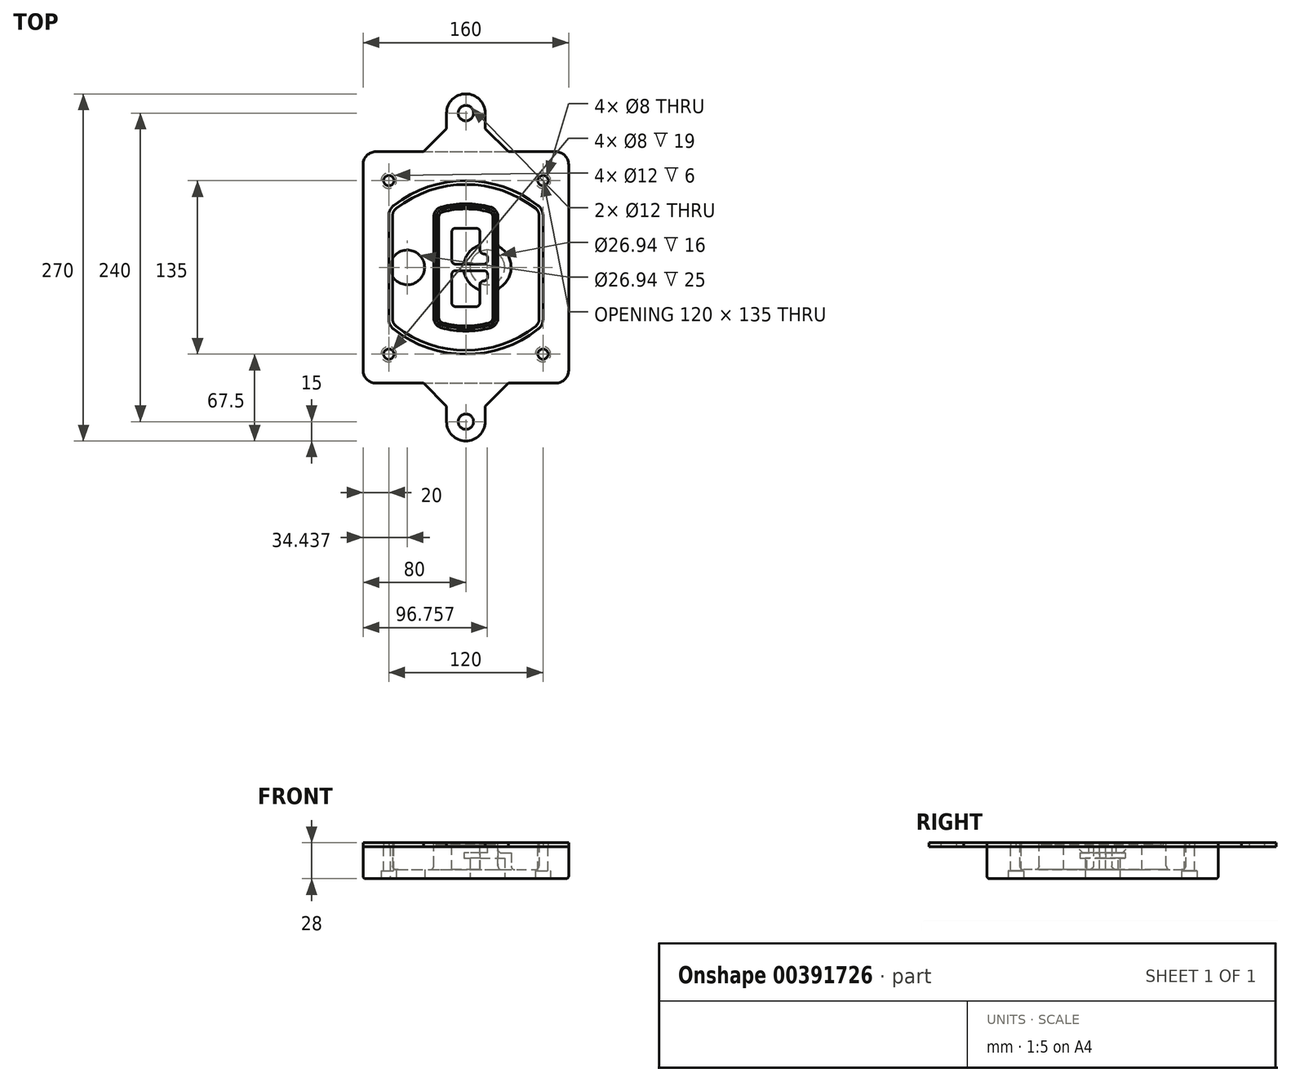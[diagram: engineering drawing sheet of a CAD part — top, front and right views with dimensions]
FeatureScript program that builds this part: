
annotation { "Feature Type Name" : "Feature", "Feature Type Description" : "" }
export const myFeature = defineFeature(function(context is Context, id is Id, definition is map)
    precondition{}
    {
        {
            var Q0;
            Q0=qCreatedBy(makeId("Top.planeOp"),FACE);
            var sketch = newSketch(context, id + "F0", { "sketchPlane" : qUnion([Q0])});
            skPoint(sketch, "E0.rect.middle", {"position": v(0, 0) * mm});
            skLineSegment(sketch, "E1.bottom", {"start": v(-70, -90) * mm, "end": v(70, -90) * mm});
            skLineSegment(sketch, "E1.top", {"start": v(-70, 90) * mm, "end": v(70, 90) * mm});
            skLineSegment(sketch, "E1.left", {"start": v(-80, -80) * mm, "end": v(-80, 80) * mm});
            skLineSegment(sketch, "E1.right", {"start": v(80, -80) * mm, "end": v(80, 80) * mm});
            skLineSegment(sketch, "E2", {"start": v(-80, 90) * mm, "end": v(80, -90) * mm, "construction": true});
            skLineSegment(sketch, "E3", {"start": v(80, 90) * mm, "end": v(-80, -90) * mm, "construction": true});
            skCircle(sketch, "E4", {"center": v(-60, 67.5) * mm, "radius": 4 * mm});
            skCircle(sketch, "E5", {"center": v(60, 67.5) * mm, "radius": 4 * mm});
            skCircle(sketch, "E6", {"center": v(60, -67.5) * mm, "radius": 4 * mm});
            skCircle(sketch, "E7", {"center": v(-60, -67.5) * mm, "radius": 4 * mm});
            skLineSegment(sketch, "E8", {"start": v(-60, 67.5) * mm, "end": v(60, 67.5) * mm, "construction": true});
            skLineSegment(sketch, "E9", {"start": v(60, 67.5) * mm, "end": v(60, -67.5) * mm, "construction": true});
            skLineSegment(sketch, "E10", {"start": v(60, -67.5) * mm, "end": v(-60, -67.5) * mm, "construction": true});
            skLineSegment(sketch, "E11", {"start": v(-60, -67.5) * mm, "end": v(-60, 67.5) * mm, "construction": true});
            skLineSegment(sketch, "E12", {"start": v(-60, 40.3) * mm, "end": v(-60, -40.3) * mm});
            skLineSegment(sketch, "E13", {"start": v(60, 40.3) * mm, "end": v(60, -40.3) * mm});
            skArc(sketch, "E14", {"start": v(56.15, 48.18) * mm, "mid": v(0, 67.5) * mm, "end": v(-56.15, 48.18) * mm});
            skArc(sketch, "E15", {"start": v(-56.15, -48.18) * mm, "mid": v(0, -67.5) * mm, "end": v(56.15, -48.18) * mm});
            skLineSegment(sketch, "E16", {"start": v(-60, 0) * mm, "end": v(60, 0) * mm, "construction": true});
            skPoint(sketch, "E17.visualSharp", {"position": v(-60, -45) * mm});
            skArc(sketch, "E17.filletArc", {"start": v(-60, -40.3) * mm, "mid": v(-58.99, -44.68) * mm, "end": v(-56.15, -48.18) * mm});
            skPoint(sketch, "E18.visualSharp", {"position": v(-60, 45) * mm});
            skArc(sketch, "E18.filletArc", {"start": v(-56.15, 48.18) * mm, "mid": v(-58.99, 44.68) * mm, "end": v(-60, 40.3) * mm});
            skPoint(sketch, "E19.visualSharp", {"position": v(60, 45) * mm});
            skArc(sketch, "E19.filletArc", {"start": v(60, 40.3) * mm, "mid": v(58.99, 44.68) * mm, "end": v(56.15, 48.18) * mm});
            skPoint(sketch, "E20.visualSharp", {"position": v(60, -45) * mm});
            skArc(sketch, "E20.filletArc", {"start": v(56.15, -48.18) * mm, "mid": v(58.99, -44.68) * mm, "end": v(60, -40.3) * mm});
            skPoint(sketch, "E21.visualSharp", {"position": v(-80, 90) * mm});
            skArc(sketch, "E21.filletArc", {"start": v(-70, 90) * mm, "mid": v(-77.07, 87.07) * mm, "end": v(-80, 80) * mm});
            skPoint(sketch, "E22.visualSharp", {"position": v(80, 90) * mm});
            skArc(sketch, "E22.filletArc", {"start": v(80, 80) * mm, "mid": v(77.07, 87.07) * mm, "end": v(70, 90) * mm});
            skPoint(sketch, "E23.visualSharp", {"position": v(80, -90) * mm});
            skArc(sketch, "E23.filletArc", {"start": v(70, -90) * mm, "mid": v(77.07, -87.07) * mm, "end": v(80, -80) * mm});
            skPoint(sketch, "E24.visualSharp", {"position": v(-80, -90) * mm});
            skArc(sketch, "E24.filletArc", {"start": v(-80, -80) * mm, "mid": v(-77.07, -87.07) * mm, "end": v(-70, -90) * mm});
            skArc(sketch, "E25.0", {"start": v(57, 40.3) * mm, "mid": v(56.3, 43.36) * mm, "end": v(54.3, 45.81) * mm});
            skLineSegment(sketch, "E25.1", {"start": v(57, 40.3) * mm, "end": v(57, -40.3) * mm});
            skArc(sketch, "E25.2", {"start": v(54.3, -45.81) * mm, "mid": v(56.3, -43.36) * mm, "end": v(57, -40.3) * mm});
            skArc(sketch, "E25.3", {"start": v(-54.3, -45.81) * mm, "mid": v(0, -64.5) * mm, "end": v(54.3, -45.81) * mm});
            skArc(sketch, "E25.4", {"start": v(-57, -40.3) * mm, "mid": v(-56.3, -43.36) * mm, "end": v(-54.3, -45.81) * mm});
            skArc(sketch, "E25.5", {"start": v(54.3, 45.81) * mm, "mid": v(0, 64.5) * mm, "end": v(-54.3, 45.81) * mm});
            skLineSegment(sketch, "E25.6", {"start": v(-57, 40.3) * mm, "end": v(-57, -40.3) * mm});
            skArc(sketch, "E25.7", {"start": v(-54.3, 45.81) * mm, "mid": v(-56.3, 43.36) * mm, "end": v(-57, 40.3) * mm});
            skArc(sketch, "E26.0", {"start": v(-58.62, 51.33) * mm, "mid": v(-62.58, 46.43) * mm, "end": v(-64, 40.3) * mm});
            skArc(sketch, "E26.1", {"start": v(58.62, 51.33) * mm, "mid": v(0, 71.5) * mm, "end": v(-58.62, 51.33) * mm});
            skArc(sketch, "E26.2", {"start": v(64, 40.3) * mm, "mid": v(62.58, 46.43) * mm, "end": v(58.62, 51.33) * mm});
            skLineSegment(sketch, "E26.3", {"start": v(64, 40.3) * mm, "end": v(64, -40.3) * mm});
            skArc(sketch, "E26.4", {"start": v(58.62, -51.33) * mm, "mid": v(62.58, -46.43) * mm, "end": v(64, -40.3) * mm});
            skLineSegment(sketch, "E26.5", {"start": v(-64, 40.3) * mm, "end": v(-64, -40.3) * mm});
            skArc(sketch, "E26.6", {"start": v(-58.62, -51.33) * mm, "mid": v(0, -71.5) * mm, "end": v(58.62, -51.33) * mm});
            skArc(sketch, "E26.7", {"start": v(-64, -40.3) * mm, "mid": v(-62.58, -46.43) * mm, "end": v(-58.62, -51.33) * mm});
            skSolve(sketch);
        }
        {
            var Q0;
            Q0=makeQuery(id+"F0.imprint","IMPRINT",FACE,{"disambiguationData":[TD([[makeQuery(id+"F0.imprint","IMPRINT",EDGE,{"derivedFrom":sQuery(id+"F0.wireOp",EDGE,"E1.bottom")}),1.0]])]});
            var Q1;
            Q1=makeQuery(id+"F0.imprint","IMPRINT",FACE,{"disambiguationData":[TD([[makeQuery(id+"F0.imprint","IMPRINT",EDGE,{"derivedFrom":sQuery(id+"F0.wireOp",EDGE,"E12")}),1.0]])]});
            var Q2;
            Q2=makeQuery(id+"F0.imprint","IMPRINT",FACE,{"disambiguationData":[TD([[makeQuery(id+"F0.imprint","IMPRINT",EDGE,{"derivedFrom":sQuery(id+"F0.wireOp",EDGE,"E25.0")}),1.0]])]});
            var Q3;
            Q3=makeQuery(id+"F0.imprint","IMPRINT",FACE,{"disambiguationData":[TD([[makeQuery(id+"F0.imprint","IMPRINT",EDGE,{"derivedFrom":sQuery(id+"F0.wireOp",EDGE,"E12")}),-1.0]])]});
            extrude(context, id + "F1", {"entities" : qUnion([Q0, Q1, Q2, Q3]), "oppositeDirection" : true, "depth" : 25 * mm});
        }
        {
            var Q0;
            Q0=makeQuery(id+"F0.imprint","IMPRINT",FACE,{"disambiguationData":[TD([[makeQuery(id+"F0.imprint","IMPRINT",EDGE,{"derivedFrom":sQuery(id+"F0.wireOp",EDGE,"E12")}),1.0]])]});
            extrude(context, id + "F2", {"entities" : qUnion([Q0]), "operationType" : NewBodyOperationType.ADD, "depth" : 3 * mm});
        }
        {
            var Q0;
            Q0=makeQuery(id+"F0.imprint","IMPRINT",FACE,{"disambiguationData":[TD([[makeQuery(id+"F0.imprint","IMPRINT",EDGE,{"derivedFrom":sQuery(id+"F0.wireOp",EDGE,"E25.0")}),1.0]])]});
            extrude(context, id + "F3", {"entities" : qUnion([Q0]), "operationType" : NewBodyOperationType.REMOVE, "oppositeDirection" : true, "depth" : 18 * mm});
        }
        {
            var Q0;
            Q0=makeQuery(id+"F2.opExtrude","CAP_FACE",FACE,{"disambiguationData":[OSD([sQuery(id+"F0.wireOp",EDGE,"E12"),sQuery(id+"F0.wireOp",EDGE,"E13"),sQuery(id+"F0.wireOp",EDGE,"E14"),sQuery(id+"F0.wireOp",EDGE,"E15"),sQuery(id+"F0.wireOp",EDGE,"E17.filletArc"),sQuery(id+"F0.wireOp",EDGE,"E18.filletArc"),sQuery(id+"F0.wireOp",EDGE,"E19.filletArc"),sQuery(id+"F0.wireOp",EDGE,"E20.filletArc"),sQuery(id+"F0.wireOp",EDGE,"E25.0"),sQuery(id+"F0.wireOp",EDGE,"E25.1"),sQuery(id+"F0.wireOp",EDGE,"E25.2"),sQuery(id+"F0.wireOp",EDGE,"E25.3"),sQuery(id+"F0.wireOp",EDGE,"E25.4"),sQuery(id+"F0.wireOp",EDGE,"E25.5"),sQuery(id+"F0.wireOp",EDGE,"E25.6"),sQuery(id+"F0.wireOp",EDGE,"E25.7")])],"isStart":false});
            var sketch = newSketch(context, id + "F4", { "sketchPlane" : qUnion([Q0])});
            skArc(sketch, "E27.0", {"start": v(-19.08, -46.97) * mm, "mid": v(0, -49.5) * mm, "end": v(19.08, -46.97) * mm});
            skArc(sketch, "E28.0", {"start": v(19.08, 46.97) * mm, "mid": v(0, 49.5) * mm, "end": v(-19.08, 46.97) * mm});
            skLineSegment(sketch, "E29", {"start": v(-25, 39.25) * mm, "end": v(-25, -39.25) * mm});
            skLineSegment(sketch, "E30", {"start": v(25, 39.25) * mm, "end": v(25, -39.25) * mm});
            skLineSegment(sketch, "E31", {"start": v(-25, 45.1) * mm, "end": v(25, 45.1) * mm, "construction": true});
            skLineSegment(sketch, "E32", {"start": v(-25, -45.1) * mm, "end": v(25, -45.1) * mm, "construction": true});
            skPoint(sketch, "E33.visualSharp", {"position": v(-25, 45.1) * mm});
            skArc(sketch, "E33.filletArc", {"start": v(-19.08, 46.97) * mm, "mid": v(-23.35, 44.11) * mm, "end": v(-25, 39.25) * mm});
            skPoint(sketch, "E34.visualSharp", {"position": v(25, 45.1) * mm});
            skArc(sketch, "E34.filletArc", {"start": v(25, 39.25) * mm, "mid": v(23.35, 44.11) * mm, "end": v(19.08, 46.97) * mm});
            skPoint(sketch, "E35.visualSharp", {"position": v(25, -45.1) * mm});
            skArc(sketch, "E35.filletArc", {"start": v(19.08, -46.97) * mm, "mid": v(23.35, -44.11) * mm, "end": v(25, -39.25) * mm});
            skPoint(sketch, "E36.visualSharp", {"position": v(-25, -45.1) * mm});
            skArc(sketch, "E36.filletArc", {"start": v(-25, -39.25) * mm, "mid": v(-23.35, -44.11) * mm, "end": v(-19.08, -46.97) * mm});
            skArc(sketch, "E37.0", {"start": v(54.3, 45.81) * mm, "mid": v(0, 64.5) * mm, "end": v(-54.3, 45.81) * mm});
            skArc(sketch, "E37.1", {"start": v(-54.3, 45.81) * mm, "mid": v(-56.3, 43.36) * mm, "end": v(-57, 40.3) * mm});
            skLineSegment(sketch, "E37.2", {"start": v(-57, 40.3) * mm, "end": v(-57, -40.3) * mm});
            skArc(sketch, "E37.3", {"start": v(-57, -40.3) * mm, "mid": v(-56.3, -43.36) * mm, "end": v(-54.3, -45.81) * mm});
            skArc(sketch, "E37.4", {"start": v(-54.3, -45.81) * mm, "mid": v(0, -64.5) * mm, "end": v(54.3, -45.81) * mm});
            skArc(sketch, "E37.5", {"start": v(54.3, -45.81) * mm, "mid": v(56.3, -43.36) * mm, "end": v(57, -40.3) * mm});
            skLineSegment(sketch, "E37.6", {"start": v(57, 40.3) * mm, "end": v(57, -40.3) * mm});
            skArc(sketch, "E37.7", {"start": v(57, 40.3) * mm, "mid": v(56.3, 43.36) * mm, "end": v(54.3, 45.81) * mm});
            skLineSegment(sketch, "E38.0", {"start": v(23, 39.25) * mm, "end": v(23, -39.25) * mm});
            skArc(sketch, "E38.1", {"start": v(18.56, -45.04) * mm, "mid": v(21.76, -42.9) * mm, "end": v(23, -39.25) * mm});
            skArc(sketch, "E38.2", {"start": v(-18.56, -45.04) * mm, "mid": v(0, -47.5) * mm, "end": v(18.56, -45.04) * mm});
            skArc(sketch, "E38.3", {"start": v(-23, -39.25) * mm, "mid": v(-21.76, -42.9) * mm, "end": v(-18.56, -45.04) * mm});
            skLineSegment(sketch, "E38.4", {"start": v(-23, 39.25) * mm, "end": v(-23, -39.25) * mm});
            skArc(sketch, "E38.5", {"start": v(23, 39.25) * mm, "mid": v(21.76, 42.9) * mm, "end": v(18.56, 45.04) * mm});
            skArc(sketch, "E38.6", {"start": v(-18.56, 45.04) * mm, "mid": v(-21.76, 42.9) * mm, "end": v(-23, 39.25) * mm});
            skArc(sketch, "E38.7", {"start": v(18.56, 45.04) * mm, "mid": v(0, 47.5) * mm, "end": v(-18.56, 45.04) * mm});
            skArc(sketch, "E39.0", {"start": v(21, 39.25) * mm, "mid": v(20.18, 41.68) * mm, "end": v(18.04, 43.1) * mm});
            skLineSegment(sketch, "E39.1", {"start": v(21, 39.25) * mm, "end": v(21, -39.25) * mm});
            skArc(sketch, "E39.2", {"start": v(18.04, -43.1) * mm, "mid": v(20.18, -41.68) * mm, "end": v(21, -39.25) * mm});
            skArc(sketch, "E39.3", {"start": v(-18.04, -43.1) * mm, "mid": v(0, -45.5) * mm, "end": v(18.04, -43.1) * mm});
            skArc(sketch, "E39.4", {"start": v(-21, -39.25) * mm, "mid": v(-20.18, -41.68) * mm, "end": v(-18.04, -43.1) * mm});
            skArc(sketch, "E39.5", {"start": v(18.04, 43.1) * mm, "mid": v(0, 45.5) * mm, "end": v(-18.04, 43.1) * mm});
            skLineSegment(sketch, "E39.6", {"start": v(-21, 39.25) * mm, "end": v(-21, -39.25) * mm});
            skArc(sketch, "E39.7", {"start": v(-18.04, 43.1) * mm, "mid": v(-20.18, 41.68) * mm, "end": v(-21, 39.25) * mm});
            skLineSegment(sketch, "E40", {"start": v(-25, 0) * mm, "end": v(25, 0) * mm, "construction": true});
            skLineSegment(sketch, "E41", {"start": v(-11, 5.5) * mm, "end": v(-11, 27.5) * mm});
            skLineSegment(sketch, "E42", {"start": v(-8, 30.5) * mm, "end": v(8, 30.5) * mm});
            skLineSegment(sketch, "E43", {"start": v(11, 27.5) * mm, "end": v(11, 13.5) * mm});
            skLineSegment(sketch, "E44", {"start": v(14, 10.5) * mm, "end": v(14, 10.5) * mm});
            skLineSegment(sketch, "E45", {"start": v(17, 7.5) * mm, "end": v(17, 5.5) * mm});
            skLineSegment(sketch, "E46", {"start": v(14, 2.5) * mm, "end": v(-8, 2.5) * mm});
            skPoint(sketch, "E47.visualSharp", {"position": v(-11, 30.5) * mm});
            skArc(sketch, "E47.filletArc", {"start": v(-8, 30.5) * mm, "mid": v(-10.12, 29.62) * mm, "end": v(-11, 27.5) * mm});
            skPoint(sketch, "E48.visualSharp", {"position": v(11, 30.5) * mm});
            skArc(sketch, "E48.filletArc", {"start": v(11, 27.5) * mm, "mid": v(10.12, 29.62) * mm, "end": v(8, 30.5) * mm});
            skPoint(sketch, "E49.visualSharp", {"position": v(11, 10.5) * mm});
            skArc(sketch, "E49.filletArc", {"start": v(11, 13.5) * mm, "mid": v(11.88, 11.38) * mm, "end": v(14, 10.5) * mm});
            skPoint(sketch, "E50.visualSharp", {"position": v(17, 10.5) * mm});
            skArc(sketch, "E50.filletArc", {"start": v(17, 7.5) * mm, "mid": v(16.12, 9.62) * mm, "end": v(14, 10.5) * mm});
            skPoint(sketch, "E51.visualSharp", {"position": v(17, 2.5) * mm});
            skArc(sketch, "E51.filletArc", {"start": v(14, 2.5) * mm, "mid": v(16.12, 3.38) * mm, "end": v(17, 5.5) * mm});
            skPoint(sketch, "E52.visualSharp", {"position": v(-11, 2.5) * mm});
            skArc(sketch, "E52.filletArc", {"start": v(-11, 5.5) * mm, "mid": v(-10.12, 3.38) * mm, "end": v(-8, 2.5) * mm});
            skLineSegment(sketch, "E53.0.MirrorCS", {"start": v(14, -2.5) * mm, "end": v(-8, -2.5) * mm});
            skArc(sketch, "E54.0.MirrorCS", {"start": v(-11, -5.5) * mm, "mid": v(-10.12, -3.38) * mm, "end": v(-8, -2.5) * mm});
            skLineSegment(sketch, "E55.0.MirrorCS", {"start": v(-11, -5.5) * mm, "end": v(-11, -27.5) * mm});
            skArc(sketch, "E56.0.MirrorCS", {"start": v(-8, -30.5) * mm, "mid": v(-10.12, -29.62) * mm, "end": v(-11, -27.5) * mm});
            skLineSegment(sketch, "E57.0.MirrorCS", {"start": v(-8, -30.5) * mm, "end": v(8, -30.5) * mm});
            skArc(sketch, "E58.0.MirrorCS", {"start": v(11, -27.5) * mm, "mid": v(10.12, -29.62) * mm, "end": v(8, -30.5) * mm});
            skLineSegment(sketch, "E59.0.MirrorCS", {"start": v(11, -27.5) * mm, "end": v(11, -13.5) * mm});
            skArc(sketch, "E60.0.MirrorCS", {"start": v(11, -13.5) * mm, "mid": v(11.88, -11.38) * mm, "end": v(14, -10.5) * mm});
            skArc(sketch, "E61.0.MirrorCS", {"start": v(17, -7.5) * mm, "mid": v(16.12, -9.62) * mm, "end": v(14, -10.5) * mm});
            skLineSegment(sketch, "E62.0.MirrorCS", {"start": v(17, -7.5) * mm, "end": v(17, -5.5) * mm});
            skArc(sketch, "E63.0.MirrorCS", {"start": v(14, -2.5) * mm, "mid": v(16.12, -3.38) * mm, "end": v(17, -5.5) * mm});
            skSolve(sketch);
        }
        {
            var Q0;
            Q0=makeQuery(id+"F4.imprint","IMPRINT",FACE,{"disambiguationData":[TD([[makeQuery(id+"F4.imprint","IMPRINT",EDGE,{"derivedFrom":sQuery(id+"F4.wireOp",EDGE,"E27.0")}),1.0]])]});
            var Q1;
            Q1=makeQuery(id+"F4.imprint","IMPRINT",FACE,{"disambiguationData":[TD([[makeQuery(id+"F4.imprint","IMPRINT",EDGE,{"derivedFrom":sQuery(id+"F4.wireOp",EDGE,"E38.0")}),-1.0]])]});
            var Q2;
            Q2=makeQuery(id+"F4.imprint","IMPRINT",FACE,{"disambiguationData":[TD([[makeQuery(id+"F4.imprint","IMPRINT",EDGE,{"derivedFrom":sQuery(id+"F4.wireOp",EDGE,"E39.0")}),1.0]])]});
            extrude(context, id + "F5", {"entities" : qUnion([Q0, Q1, Q2]), "operationType" : NewBodyOperationType.ADD, "endBound" : BoundingType.UP_TO_NEXT, "oppositeDirection" : true, "depth" : 25 * mm});
        }
        {
            var Q0;
            Q0=makeQuery(id+"F4.imprint","IMPRINT",FACE,{"disambiguationData":[TD([[makeQuery(id+"F4.imprint","IMPRINT",EDGE,{"derivedFrom":sQuery(id+"F4.wireOp",EDGE,"E38.0")}),-1.0]])]});
            extrude(context, id + "F6", {"entities" : qUnion([Q0]), "operationType" : NewBodyOperationType.REMOVE, "oppositeDirection" : true, "depth" : 2 * mm});
        }
        {
            var Q0;
            Q0=makeQuery(id+"F1.opExtrude","CAP_FACE",FACE,{"disambiguationData":[OSD([sQuery(id+"F0.wireOp",EDGE,"E1.bottom"),sQuery(id+"F0.wireOp",EDGE,"E1.top"),sQuery(id+"F0.wireOp",EDGE,"E1.left"),sQuery(id+"F0.wireOp",EDGE,"E1.right"),sQuery(id+"F0.wireOp",EDGE,"E4"),sQuery(id+"F0.wireOp",EDGE,"E5"),sQuery(id+"F0.wireOp",EDGE,"E6"),sQuery(id+"F0.wireOp",EDGE,"E7"),sQuery(id+"F0.wireOp",EDGE,"E21.filletArc"),sQuery(id+"F0.wireOp",EDGE,"E22.filletArc"),sQuery(id+"F0.wireOp",EDGE,"E23.filletArc"),sQuery(id+"F0.wireOp",EDGE,"E24.filletArc")])],"isStart":false});
            var sketch = newSketch(context, id + "F7", { "sketchPlane" : qUnion([Q0])});
            skCircle(sketch, "E64", {"center": v(16.76, 0) * mm, "radius": 13.47 * mm});
            skCircle(sketch, "E65", {"center": v(-45.56, 0) * mm, "radius": 13.47 * mm});
            skLineSegment(sketch, "E66", {"start": v(80, 0) * mm, "end": v(-80, 0) * mm});
            skCircle(sketch, "E67", {"center": v(16.76, 0) * mm, "radius": 18.47 * mm});
            skCircle(sketch, "E68", {"center": v(60, -67.5) * mm, "radius": 6 * mm});
            skCircle(sketch, "E69", {"center": v(-60, -67.5) * mm, "radius": 6 * mm});
            skCircle(sketch, "E70", {"center": v(-60, 67.5) * mm, "radius": 6 * mm});
            skCircle(sketch, "E71", {"center": v(60, 67.5) * mm, "radius": 6 * mm});
            skSolve(sketch);
        }
        {
            var Q0;
            {var subQ1=sQuery(id+"F7.wireOp",EDGE,"E66");var subQ4=sQuery(id+"F7.wireOp",EDGE,"E64");var subQ6=makeQuery(id+"F7.imprint","INTERSECT",VERTEX,{"disambiguationData":[OD(0.0)],"derivedFrom":[subQ4,subQ1]});Q0=makeQuery(id+"F7.imprint","IMPRINT",FACE,{"disambiguationData":[TD([[makeQuery(id+"F7.imprint","IMPRINT",EDGE,{"disambiguationData":[TD([[subQ6,-1.0]])],"derivedFrom":subQ4}),-1.0]])]});}
            var Q1;
            {var subQ0=sQuery(id+"F7.wireOp",EDGE,"E66");var subQ1=sQuery(id+"F7.wireOp",EDGE,"E64");var subQ3=makeQuery(id+"F7.imprint","INTERSECT",VERTEX,{"disambiguationData":[OD(0.0)],"derivedFrom":[subQ1,subQ0]});Q1=makeQuery(id+"F7.imprint","IMPRINT",FACE,{"disambiguationData":[TD([[makeQuery(id+"F7.imprint","IMPRINT",EDGE,{"disambiguationData":[TD([[subQ3,-1.0]])],"derivedFrom":subQ1}),1.0]])]});}
            var Q2;
            {var subQ0=sQuery(id+"F7.wireOp",EDGE,"E66");var subQ1=sQuery(id+"F7.wireOp",EDGE,"E64");var subQ3=makeQuery(id+"F7.imprint","INTERSECT",VERTEX,{"disambiguationData":[OD(0.0)],"derivedFrom":[subQ1,subQ0]});Q2=makeQuery(id+"F7.imprint","IMPRINT",FACE,{"disambiguationData":[TD([[makeQuery(id+"F7.imprint","IMPRINT",EDGE,{"disambiguationData":[TD([[subQ3,1.0]])],"derivedFrom":subQ1}),1.0]])]});}
            var Q3;
            {var subQ1=sQuery(id+"F7.wireOp",EDGE,"E66");var subQ4=sQuery(id+"F7.wireOp",EDGE,"E64");var subQ6=makeQuery(id+"F7.imprint","INTERSECT",VERTEX,{"disambiguationData":[OD(0.0)],"derivedFrom":[subQ4,subQ1]});Q3=makeQuery(id+"F7.imprint","IMPRINT",FACE,{"disambiguationData":[TD([[makeQuery(id+"F7.imprint","IMPRINT",EDGE,{"disambiguationData":[TD([[subQ6,1.0]])],"derivedFrom":subQ4}),-1.0]])]});}
            extrude(context, id + "F8", {"entities" : qUnion([Q0, Q1, Q2, Q3]), "operationType" : NewBodyOperationType.ADD, "oppositeDirection" : true, "depth" : 20 * mm});
        }
        {
            var Q0;
            {var subQ0=sQuery(id+"F7.wireOp",EDGE,"E66");var subQ1=sQuery(id+"F7.wireOp",EDGE,"E64");var subQ3=makeQuery(id+"F7.imprint","INTERSECT",VERTEX,{"disambiguationData":[OD(0.0)],"derivedFrom":[subQ1,subQ0]});Q0=makeQuery(id+"F7.imprint","IMPRINT",FACE,{"disambiguationData":[TD([[makeQuery(id+"F7.imprint","IMPRINT",EDGE,{"disambiguationData":[TD([[subQ3,-1.0]])],"derivedFrom":subQ1}),1.0]])]});}
            var Q1;
            {var subQ0=sQuery(id+"F7.wireOp",EDGE,"E66");var subQ1=sQuery(id+"F7.wireOp",EDGE,"E64");var subQ3=makeQuery(id+"F7.imprint","INTERSECT",VERTEX,{"disambiguationData":[OD(0.0)],"derivedFrom":[subQ1,subQ0]});Q1=makeQuery(id+"F7.imprint","IMPRINT",FACE,{"disambiguationData":[TD([[makeQuery(id+"F7.imprint","IMPRINT",EDGE,{"disambiguationData":[TD([[subQ3,1.0]])],"derivedFrom":subQ1}),1.0]])]});}
            extrude(context, id + "F9", {"entities" : qUnion([Q0, Q1]), "operationType" : NewBodyOperationType.REMOVE, "oppositeDirection" : true, "depth" : 16 * mm});
        }
        {
            var Q0;
            {var subQ0=sQuery(id+"F7.wireOp",EDGE,"E66");var subQ1=sQuery(id+"F7.wireOp",EDGE,"E65");var subQ3=makeQuery(id+"F7.imprint","INTERSECT",VERTEX,{"disambiguationData":[OD(0.0)],"derivedFrom":[subQ1,subQ0]});Q0=makeQuery(id+"F7.imprint","IMPRINT",FACE,{"disambiguationData":[TD([[makeQuery(id+"F7.imprint","IMPRINT",EDGE,{"disambiguationData":[TD([[subQ3,-1.0]])],"derivedFrom":subQ1}),1.0]])]});}
            var Q1;
            {var subQ0=sQuery(id+"F7.wireOp",EDGE,"E66");var subQ1=sQuery(id+"F7.wireOp",EDGE,"E65");var subQ3=makeQuery(id+"F7.imprint","INTERSECT",VERTEX,{"disambiguationData":[OD(0.0)],"derivedFrom":[subQ1,subQ0]});Q1=makeQuery(id+"F7.imprint","IMPRINT",FACE,{"disambiguationData":[TD([[makeQuery(id+"F7.imprint","IMPRINT",EDGE,{"disambiguationData":[TD([[subQ3,1.0]])],"derivedFrom":subQ1}),1.0]])]});}
            extrude(context, id + "F10", {"entities" : qUnion([Q0, Q1]), "operationType" : NewBodyOperationType.REMOVE, "oppositeDirection" : true, "depth" : 25 * mm});
        }
        {
            var Q0;
            Q0=makeQuery(id+"F7.imprint","IMPRINT",FACE,{"disambiguationData":[TD([[makeQuery(id+"F7.imprint","IMPRINT",EDGE,{"derivedFrom":sQuery(id+"F7.wireOp",EDGE,"E68")}),1.0]])]});
            var Q1;
            Q1=makeQuery(id+"F7.imprint","IMPRINT",FACE,{"disambiguationData":[TD([[makeQuery(id+"F7.imprint","IMPRINT",EDGE,{"derivedFrom":makeQuery(id+"F1.opExtrude","CAP_EDGE",EDGE,{"disambiguationData":[OSD([sQuery(id+"F0.wireOp",EDGE,"E5")])],"isStart":false})}),-1.0]])]});
            var Q2;
            Q2=makeQuery(id+"F7.imprint","IMPRINT",FACE,{"disambiguationData":[TD([[makeQuery(id+"F7.imprint","IMPRINT",EDGE,{"derivedFrom":sQuery(id+"F7.wireOp",EDGE,"E69")}),1.0]])]});
            var Q3;
            Q3=makeQuery(id+"F7.imprint","IMPRINT",FACE,{"disambiguationData":[TD([[makeQuery(id+"F7.imprint","IMPRINT",EDGE,{"derivedFrom":makeQuery(id+"F1.opExtrude","CAP_EDGE",EDGE,{"disambiguationData":[OSD([sQuery(id+"F0.wireOp",EDGE,"E4")])],"isStart":false})}),-1.0]])]});
            var Q4;
            Q4=makeQuery(id+"F7.imprint","IMPRINT",FACE,{"disambiguationData":[TD([[makeQuery(id+"F7.imprint","IMPRINT",EDGE,{"derivedFrom":sQuery(id+"F7.wireOp",EDGE,"E70")}),1.0]])]});
            var Q5;
            Q5=makeQuery(id+"F7.imprint","IMPRINT",FACE,{"disambiguationData":[TD([[makeQuery(id+"F7.imprint","IMPRINT",EDGE,{"derivedFrom":makeQuery(id+"F1.opExtrude","CAP_EDGE",EDGE,{"disambiguationData":[OSD([sQuery(id+"F0.wireOp",EDGE,"E7")])],"isStart":false})}),-1.0]])]});
            var Q6;
            Q6=makeQuery(id+"F7.imprint","IMPRINT",FACE,{"disambiguationData":[TD([[makeQuery(id+"F7.imprint","IMPRINT",EDGE,{"derivedFrom":sQuery(id+"F7.wireOp",EDGE,"E71")}),1.0]])]});
            var Q7;
            Q7=makeQuery(id+"F7.imprint","IMPRINT",FACE,{"disambiguationData":[TD([[makeQuery(id+"F7.imprint","IMPRINT",EDGE,{"derivedFrom":makeQuery(id+"F1.opExtrude","CAP_EDGE",EDGE,{"disambiguationData":[OSD([sQuery(id+"F0.wireOp",EDGE,"E6")])],"isStart":false})}),-1.0]])]});
            extrude(context, id + "F11", {"entities" : qUnion([Q0, Q1, Q2, Q3, Q4, Q5, Q6, Q7]), "operationType" : NewBodyOperationType.REMOVE, "oppositeDirection" : true, "depth" : 6 * mm});
        }
        {
            var Q0;
            Q0=makeQuery(id+"F9.boolean.opBoolean","COPY",FACE,{"derivedFrom":makeQuery(id+"F9.opExtrude","CAP_FACE",FACE,{"disambiguationData":[OSD([sQuery(id+"F7.wireOp",EDGE,"E64")])],"isStart":false})});
            var sketch = newSketch(context, id + "F12", { "sketchPlane" : qUnion([Q0])});
            skArc(sketch, "E72.0", {"start": v(11, 17.55) * mm, "mid": v(2.57, 11.82) * mm, "end": v(-1.54, 2.5) * mm});
            skArc(sketch, "E72.1", {"start": v(-1.54, -2.5) * mm, "mid": v(2.57, -11.82) * mm, "end": v(11, -17.55) * mm});
            skLineSegment(sketch, "E73", {"start": v(-1.54, -2.5) * mm, "end": v(14, -2.5) * mm});
            skLineSegment(sketch, "E74.0", {"start": v(14, 2.5) * mm, "end": v(-1.54, 2.5) * mm});
            skArc(sketch, "E74.1", {"start": v(14, 2.5) * mm, "mid": v(16.12, 3.38) * mm, "end": v(17, 5.5) * mm});
            skLineSegment(sketch, "E74.2", {"start": v(17, 7.5) * mm, "end": v(17, 5.5) * mm});
            skArc(sketch, "E74.3", {"start": v(17, 7.5) * mm, "mid": v(16.12, 9.62) * mm, "end": v(14, 10.5) * mm});
            skArc(sketch, "E74.4", {"start": v(11, 13.5) * mm, "mid": v(11.88, 11.38) * mm, "end": v(14, 10.5) * mm});
            skLineSegment(sketch, "E74.5", {"start": v(11, 17.55) * mm, "end": v(11, 13.5) * mm});
            skLineSegment(sketch, "E74.7", {"start": v(14, -2.5) * mm, "end": v(-1.54, -2.5) * mm});
            skArc(sketch, "E74.8", {"start": v(14, -2.5) * mm, "mid": v(16.12, -3.38) * mm, "end": v(17, -5.5) * mm});
            skLineSegment(sketch, "E74.9", {"start": v(17, -7.5) * mm, "end": v(17, -5.5) * mm});
            skArc(sketch, "E74.10", {"start": v(17, -7.5) * mm, "mid": v(16.12, -9.62) * mm, "end": v(14, -10.5) * mm});
            skArc(sketch, "E74.11", {"start": v(11, -13.5) * mm, "mid": v(11.88, -11.38) * mm, "end": v(14, -10.5) * mm});
            skLineSegment(sketch, "E74.12", {"start": v(11, -17.55) * mm, "end": v(11, -13.5) * mm});
            skPoint(sketch, "E75.orphan", {"position": v(11, -27.5) * mm});
            skPoint(sketch, "E76.orphan", {"position": v(-8, -2.5) * mm});
            skPoint(sketch, "E77.orphan", {"position": v(-8, 2.5) * mm});
            skPoint(sketch, "E78.orphan", {"position": v(11, 27.5) * mm});
            skSolve(sketch);
        }
        {
            var Q0;
            {var subQ7=sQuery(id+"F12.wireOp",EDGE,"E72.0");var subQ14=sQuery(id+"F12.wireOp",EDGE,"E72.1");var subQ16=sQuery(id+"F12.wireOp",EDGE,"E74.1");var subQ18=sQuery(id+"F12.wireOp",EDGE,"E74.8");Q0=qUnion([makeQuery(id+"F12.imprint","IMPRINT",FACE,{"disambiguationData":[TD([[makeQuery(id+"F12.imprint","IMPRINT",EDGE,{"derivedFrom":subQ7}),1.0]])]}),makeQuery(id+"F12.imprint","IMPRINT",FACE,{"disambiguationData":[TD([[makeQuery(id+"F12.imprint","IMPRINT",EDGE,{"derivedFrom":subQ14}),1.0]])]}),makeQuery(id+"F12.imprint","IMPRINT",FACE,{"disambiguationData":[TD([[makeQuery(id+"F12.imprint","IMPRINT",EDGE,{"derivedFrom":subQ16}),1.0]])]}),makeQuery(id+"F12.imprint","IMPRINT",FACE,{"disambiguationData":[TD([[makeQuery(id+"F12.imprint","IMPRINT",EDGE,{"derivedFrom":subQ18}),-1.0]])]})]);}
            var Q1;
            Q1=makeQuery(id+"F5.boolean.opBoolean","SPLIT",FACE,{"disambiguationData":[TD([makeQuery(id+"F5.opExtrude","SWEPT_FACE",FACE,{"disambiguationData":[OSD([sQuery(id+"F4.wireOp",EDGE,"E41")])]})])],"derivedFrom":makeQuery(id+"F3.boolean.opBoolean","COPY",FACE,{"derivedFrom":makeQuery(id+"F3.opExtrude","CAP_FACE",FACE,{"disambiguationData":[OSD([sQuery(id+"F0.wireOp",EDGE,"E25.0"),sQuery(id+"F0.wireOp",EDGE,"E25.1"),sQuery(id+"F0.wireOp",EDGE,"E25.2"),sQuery(id+"F0.wireOp",EDGE,"E25.3"),sQuery(id+"F0.wireOp",EDGE,"E25.4"),sQuery(id+"F0.wireOp",EDGE,"E25.5"),sQuery(id+"F0.wireOp",EDGE,"E25.6"),sQuery(id+"F0.wireOp",EDGE,"E25.7")])],"isStart":false})})});
            extrude(context, id + "F13", {"entities" : qUnion([Q0]), "operationType" : NewBodyOperationType.REMOVE, "endBound" : BoundingType.UP_TO_SURFACE, "endBoundEntityFace" : qUnion([Q1]), "depth" : 25 * mm});
        }
        {
            var Q0;
            Q0=makeQuery(id+"F3.boolean.opBoolean","COPY",EDGE,{"derivedFrom":makeQuery(id+"F3.opExtrude","CAP_EDGE",EDGE,{"disambiguationData":[OSD([sQuery(id+"F0.wireOp",EDGE,"E25.6")])],"isStart":false})});
            var Q1;
            Q1=makeQuery(id+"F8.boolean.opBoolean","INTERSECT",EDGE,{"derivedFrom":[makeQuery(id+"F5.opExtrude","SWEPT_FACE",FACE,{"disambiguationData":[OSD([sQuery(id+"F4.wireOp",EDGE,"E30")])]}),makeQuery(id+"F8.opExtrude","CAP_FACE",FACE,{"disambiguationData":[OSD([sQuery(id+"F7.wireOp",EDGE,"E67")])],"isStart":false})]});
            var Q2;
            Q2=makeQuery(id+"F8.boolean.opBoolean","INTERSECT",EDGE,{"disambiguationData":[OD(1.0)],"derivedFrom":[makeQuery(id+"F5.opExtrude","SWEPT_FACE",FACE,{"disambiguationData":[OSD([sQuery(id+"F4.wireOp",EDGE,"E30")])]}),makeQuery(id+"F8.opExtrude","SWEPT_FACE",FACE,{"disambiguationData":[OSD([sQuery(id+"F7.wireOp",EDGE,"E67")])]})]});
            var Q3;
            {var subQ0=sQuery(id+"F4.wireOp",EDGE,"E30");Q3=makeQuery(id+"F8.boolean.opBoolean","SPLIT",EDGE,{"disambiguationData":[TD([makeQuery(id+"F5.opExtrude","SWEPT_FACE",FACE,{"disambiguationData":[OSD([sQuery(id+"F4.wireOp",EDGE,"E35.filletArc")])]})])],"derivedFrom":makeQuery(id+"F5.opExtrude","CAP_EDGE",EDGE,{"disambiguationData":[OSD([subQ0])],"isStart":false})});}
            var Q4;
            {var subQ0=sQuery(id+"F0.wireOp",EDGE,"E25.7");var subQ1=sQuery(id+"F0.wireOp",EDGE,"E25.1");var subQ2=sQuery(id+"F0.wireOp",EDGE,"E25.6");var subQ3=sQuery(id+"F0.wireOp",EDGE,"E25.5");var subQ4=sQuery(id+"F0.wireOp",EDGE,"E25.4");var subQ5=sQuery(id+"F0.wireOp",EDGE,"E25.0");var subQ6=sQuery(id+"F0.wireOp",EDGE,"E25.2");var subQ7=sQuery(id+"F0.wireOp",EDGE,"E25.3");Q4=makeQuery(id+"F8.boolean.opBoolean","INTERSECT",EDGE,{"derivedFrom":[makeQuery(id+"F5.boolean.opBoolean","SPLIT",FACE,{"disambiguationData":[TD([makeQuery(id+"F2.opExtrude","SWEPT_FACE",FACE,{"disambiguationData":[OSD([subQ5])]})])],"derivedFrom":makeQuery(id+"F3.boolean.opBoolean","COPY",FACE,{"derivedFrom":makeQuery(id+"F3.opExtrude","CAP_FACE",FACE,{"disambiguationData":[OSD([subQ5,subQ1,subQ6,subQ7,subQ4,subQ3,subQ2,subQ0])],"isStart":false})})}),makeQuery(id+"F8.opExtrude","SWEPT_FACE",FACE,{"disambiguationData":[OSD([sQuery(id+"F7.wireOp",EDGE,"E67")])]})]});}
            var Q5;
            Q5=makeQuery(id+"F8.boolean.opBoolean","INTERSECT",EDGE,{"disambiguationData":[OD(0.0)],"derivedFrom":[makeQuery(id+"F5.opExtrude","SWEPT_FACE",FACE,{"disambiguationData":[OSD([sQuery(id+"F4.wireOp",EDGE,"E30")])]}),makeQuery(id+"F8.opExtrude","SWEPT_FACE",FACE,{"disambiguationData":[OSD([sQuery(id+"F7.wireOp",EDGE,"E67")])]})]});
            fillet(context, id + "F14", {"entities" : qUnion([Q0, Q1, Q2, Q3, Q4, Q5]), "radius" : 3 * mm, "tangentPropagation" : true, "allowEdgeOverflow" : false});
        }
        {
            var Q0;
            Q0=makeQuery(id+"F1.opExtrude","CAP_EDGE",EDGE,{"disambiguationData":[OSD([sQuery(id+"F0.wireOp",EDGE,"E1.bottom")])],"isStart":false});
            fillet(context, id + "F15", {"entities" : qUnion([Q0]), "radius" : 2 * mm, "tangentPropagation" : true, "allowEdgeOverflow" : false});
        }
        {
            var Q0;
            {var subQ0=sQuery(id+"F0.wireOp",EDGE,"E21.filletArc");var subQ1=sQuery(id+"F0.wireOp",EDGE,"E7");var subQ2=sQuery(id+"F0.wireOp",EDGE,"E6");var subQ3=sQuery(id+"F0.wireOp",EDGE,"E5");var subQ4=sQuery(id+"F0.wireOp",EDGE,"E4");var subQ5=sQuery(id+"F0.wireOp",EDGE,"E22.filletArc");var subQ6=sQuery(id+"F0.wireOp",EDGE,"E1.bottom");var subQ7=sQuery(id+"F0.wireOp",EDGE,"E1.right");var subQ8=sQuery(id+"F0.wireOp",EDGE,"E1.top");var subQ9=sQuery(id+"F0.wireOp",EDGE,"E1.left");var subQ10=sQuery(id+"F0.wireOp",EDGE,"E23.filletArc");var subQ11=sQuery(id+"F0.wireOp",EDGE,"E24.filletArc");Q0=makeQuery(id+"F2.boolean.opBoolean","SPLIT",FACE,{"disambiguationData":[TD([makeQuery(id+"F1.opExtrude","SWEPT_FACE",FACE,{"disambiguationData":[OSD([subQ6])]})])],"derivedFrom":makeQuery(id+"F1.opExtrude","CAP_FACE",FACE,{"disambiguationData":[OSD([subQ6,subQ8,subQ9,subQ7,subQ4,subQ3,subQ2,subQ1,subQ0,subQ5,subQ10,subQ11])],"isStart":true})});}
            var sketch = newSketch(context, id + "F16", { "sketchPlane" : qUnion([Q0])});
            skLineSegment(sketch, "E79", {"start": v(0, 90) * mm, "end": v(0, 120) * mm, "construction": true});
            skArc(sketch, "E80", {"start": v(15, 120) * mm, "mid": v(0, 135) * mm, "end": v(-15, 120) * mm});
            skLineSegment(sketch, "E81", {"start": v(-15, 120) * mm, "end": v(-15, 108) * mm});
            skLineSegment(sketch, "E82", {"start": v(15, 120) * mm, "end": v(15, 108) * mm});
            skLineSegment(sketch, "E83", {"start": v(-15, 108) * mm, "end": v(-33, 90) * mm});
            skLineSegment(sketch, "E84", {"start": v(15, 108) * mm, "end": v(33, 90) * mm});
            skCircle(sketch, "E85", {"center": v(0, 120) * mm, "radius": 6 * mm});
            skLineSegment(sketch, "E86", {"start": v(0, -90) * mm, "end": v(0, -116.25) * mm, "construction": true});
            skArc(sketch, "E87.MirrorCS", {"start": v(-15, 120) * mm, "mid": v(0, 135) * mm, "end": v(15, 120) * mm});
            skLineSegment(sketch, "E88", {"start": v(-122.35, 0) * mm, "end": v(123.7, 0) * mm, "construction": true});
            skPoint(sketch, "E88.endSnap0", {"position": v(80, 0) * mm});
            skLineSegment(sketch, "E89.MirrorCS", {"start": v(-15, -120) * mm, "end": v(-15, -108) * mm});
            skLineSegment(sketch, "E90.MirrorCS", {"start": v(15, -120) * mm, "end": v(15, -108) * mm});
            skLineSegment(sketch, "E91.MirrorCS", {"start": v(15, -108) * mm, "end": v(33, -90) * mm});
            skLineSegment(sketch, "E92.MirrorCS", {"start": v(-15, -108) * mm, "end": v(-33, -90) * mm});
            skArc(sketch, "E93.MirrorCS", {"start": v(-15, -120) * mm, "mid": v(0, -135) * mm, "end": v(15, -120) * mm});
            skCircle(sketch, "E94.MirrorC", {"center": v(0, -120) * mm, "radius": 6 * mm});
            skArc(sketch, "E95.MirrorCS", {"start": v(15, -120) * mm, "mid": v(0, -135) * mm, "end": v(-15, -120) * mm});
            skLineSegment(sketch, "E96.MirrorCS", {"start": v(0, -90) * mm, "end": v(0, -120) * mm, "construction": true});
            skSolve(sketch);
        }
        {
            var Q0;
            Q0=makeQuery(id+"F16.imprint","IMPRINT",FACE,{"disambiguationData":[TD([[makeQuery(id+"F16.imprint","IMPRINT",EDGE,{"derivedFrom":sQuery(id+"F16.wireOp",EDGE,"E81")}),1.0]])]});
            var Q1;
            Q1=makeQuery(id+"F16.imprint","IMPRINT",FACE,{"disambiguationData":[TD([[makeQuery(id+"F16.imprint","IMPRINT",EDGE,{"derivedFrom":sQuery(id+"F16.wireOp",EDGE,"E90.MirrorCS")}),1.0]])]});
            var Q2;
            Q2=makeQuery(id+"F16.imprint","IMPRINT",FACE,{"disambiguationData":[TD([[makeQuery(id+"F16.imprint","IMPRINT",EDGE,{"derivedFrom":makeQuery(id+"F1.opExtrude","CAP_EDGE",EDGE,{"disambiguationData":[OSD([sQuery(id+"F0.wireOp",EDGE,"E1.left")])],"isStart":true})}),-1.0]])]});
            var Q3;
            Q3=makeQuery(id+"F2.opExtrude","CAP_FACE",FACE,{"disambiguationData":[OSD([sQuery(id+"F0.wireOp",EDGE,"E12"),sQuery(id+"F0.wireOp",EDGE,"E13"),sQuery(id+"F0.wireOp",EDGE,"E14"),sQuery(id+"F0.wireOp",EDGE,"E15"),sQuery(id+"F0.wireOp",EDGE,"E17.filletArc"),sQuery(id+"F0.wireOp",EDGE,"E18.filletArc"),sQuery(id+"F0.wireOp",EDGE,"E19.filletArc"),sQuery(id+"F0.wireOp",EDGE,"E20.filletArc"),sQuery(id+"F0.wireOp",EDGE,"E25.0"),sQuery(id+"F0.wireOp",EDGE,"E25.1"),sQuery(id+"F0.wireOp",EDGE,"E25.2"),sQuery(id+"F0.wireOp",EDGE,"E25.3"),sQuery(id+"F0.wireOp",EDGE,"E25.4"),sQuery(id+"F0.wireOp",EDGE,"E25.5"),sQuery(id+"F0.wireOp",EDGE,"E25.6"),sQuery(id+"F0.wireOp",EDGE,"E25.7")])],"isStart":false});
            extrude(context, id + "F17", {"entities" : qUnion([Q0, Q1, Q2]), "endBound" : BoundingType.UP_TO_SURFACE, "endBoundEntityFace" : qUnion([Q3]), "depth" : 25 * mm});
        }
    });
